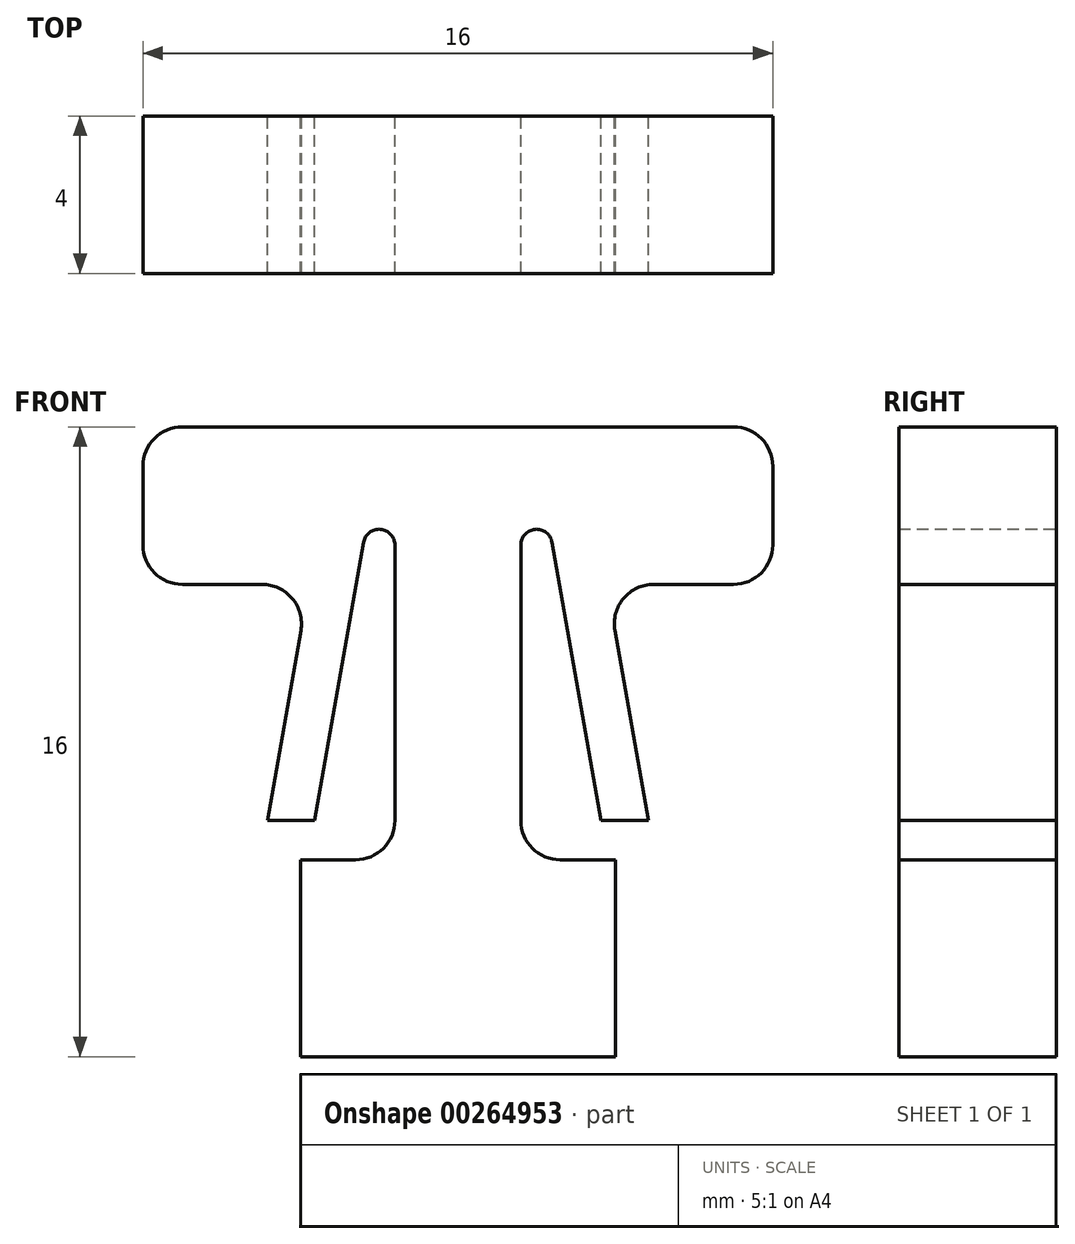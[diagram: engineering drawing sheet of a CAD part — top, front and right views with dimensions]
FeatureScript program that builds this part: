
annotation { "Feature Type Name" : "Feature", "Feature Type Description" : "" }
export const myFeature = defineFeature(function(context is Context, id is Id, definition is map)
    precondition{}
    {
        {
            var Q0;
            Q0=qCreatedBy(makeId("Front.planeOp"),FACE);
            var sketch = newSketch(context, id + "F0", { "sketchPlane" : qUnion([Q0])});
            skLineSegment(sketch, "E0", {"start": v(0, 0) * mm, "end": v(0, 25.15) * mm, "construction": true});
            skLineSegment(sketch, "E1", {"start": v(8, 16) * mm, "end": v(8, 12) * mm});
            skLineSegment(sketch, "E2", {"start": v(4.97, 12) * mm, "end": v(8, 12) * mm});
            skLineSegment(sketch, "E3", {"start": v(4, 0) * mm, "end": v(0, 0) * mm});
            skLineSegment(sketch, "E4", {"start": v(3.99, 10.83) * mm, "end": v(4.84, 6) * mm});
            skLineSegment(sketch, "E5", {"start": v(4.84, 6) * mm, "end": v(3.64, 6) * mm});
            skLineSegment(sketch, "E6", {"start": v(3.64, 6) * mm, "end": v(2.4, 13.07) * mm});
            skLineSegment(sketch, "E7", {"start": v(1.6, 13) * mm, "end": v(1.6, 5) * mm});
            skLineSegment(sketch, "E8", {"start": v(1.6, 5) * mm, "end": v(4, 5) * mm});
            skLineSegment(sketch, "E9", {"start": v(4, 5) * mm, "end": v(4, 0) * mm});
            skLineSegment(sketch, "E10", {"start": v(8, 16) * mm, "end": v(0, 16) * mm});
            skLineSegment(sketch, "E11.MirrorCS", {"start": v(-8, 16) * mm, "end": v(0, 16) * mm});
            skLineSegment(sketch, "E12.MirrorCS", {"start": v(-8, 16) * mm, "end": v(-8, 12) * mm});
            skLineSegment(sketch, "E13.MirrorCS", {"start": v(-4.97, 12) * mm, "end": v(-8, 12) * mm});
            skLineSegment(sketch, "E14.MirrorCS", {"start": v(-3.99, 10.83) * mm, "end": v(-4.84, 6) * mm});
            skLineSegment(sketch, "E15.MirrorCS", {"start": v(-4.84, 6) * mm, "end": v(-3.64, 6) * mm});
            skLineSegment(sketch, "E16.MirrorCS", {"start": v(-3.64, 6) * mm, "end": v(-2.4, 13.07) * mm});
            skLineSegment(sketch, "E17.MirrorCS", {"start": v(-1.6, 13) * mm, "end": v(-1.6, 5) * mm});
            skLineSegment(sketch, "E18.MirrorCS", {"start": v(-1.6, 5) * mm, "end": v(-4, 5) * mm});
            skLineSegment(sketch, "E19.MirrorCS", {"start": v(-4, 5) * mm, "end": v(-4, 0) * mm});
            skLineSegment(sketch, "E20.MirrorCS", {"start": v(-4, 0) * mm, "end": v(0, 0) * mm});
            skPoint(sketch, "E21.newPointA", {"position": v(-2.58, 12) * mm});
            skPoint(sketch, "E21.newPointB", {"position": v(-1.6, 20) * mm});
            skArc(sketch, "E21.filletArc", {"start": v(-1.6, 13) * mm, "mid": v(-1.97, 13.4) * mm, "end": v(-2.4, 13.07) * mm});
            skPoint(sketch, "E22.newPointA", {"position": v(1.6, 20) * mm});
            skPoint(sketch, "E22.newPointB", {"position": v(2.58, 12) * mm});
            skArc(sketch, "E22.filletArc", {"start": v(2.4, 13.07) * mm, "mid": v(1.97, 13.4) * mm, "end": v(1.6, 13) * mm});
            skPoint(sketch, "E23.visualSharp", {"position": v(-3.78, 12) * mm});
            skArc(sketch, "E23.filletArc", {"start": v(-3.99, 10.83) * mm, "mid": v(-4.2, 11.64) * mm, "end": v(-4.97, 12) * mm});
            skPoint(sketch, "E24.visualSharp", {"position": v(3.78, 12) * mm});
            skArc(sketch, "E24.filletArc", {"start": v(4.97, 12) * mm, "mid": v(4.2, 11.64) * mm, "end": v(3.99, 10.83) * mm});
            skLineSegment(sketch, "E25", {"start": v(-2, 13) * mm, "end": v(2, 13) * mm, "construction": true});
            skSolve(sketch);
        }
        {
            var Q0;
            Q0 = qSketchRegion(id + "F0", true);
            extrude(context, id + "F1", {"entities" : qUnion([Q0]), "depth" : 4 * mm});
        }
        {
            var Q0;
            Q0=makeQuery(id+"F1.opExtrude","SWEPT_EDGE",EDGE,{"disambiguationData":[OSD([sQuery(id+"F0.wireOp",EDGE,"E1"),sQuery(id+"F0.wireOp",EDGE,"E2")])]});
            var Q1;
            Q1=makeQuery(id+"F1.opExtrude","SWEPT_EDGE",EDGE,{"disambiguationData":[OSD([sQuery(id+"F0.wireOp",EDGE,"E1"),sQuery(id+"F0.wireOp",EDGE,"E10")])]});
            var Q2;
            Q2=makeQuery(id+"F1.opExtrude","SWEPT_EDGE",EDGE,{"disambiguationData":[OSD([sQuery(id+"F0.wireOp",EDGE,"E12.MirrorCS"),sQuery(id+"F0.wireOp",EDGE,"E13.MirrorCS")])]});
            var Q3;
            Q3=makeQuery(id+"F1.opExtrude","SWEPT_EDGE",EDGE,{"disambiguationData":[OSD([sQuery(id+"F0.wireOp",EDGE,"E11.MirrorCS"),sQuery(id+"F0.wireOp",EDGE,"E12.MirrorCS")])]});
            var Q4;
            Q4=makeQuery(id+"F1.opExtrude","SWEPT_EDGE",EDGE,{"disambiguationData":[OSD([sQuery(id+"F0.wireOp",EDGE,"E7"),sQuery(id+"F0.wireOp",EDGE,"E8")])]});
            var Q5;
            Q5=makeQuery(id+"F1.opExtrude","SWEPT_EDGE",EDGE,{"disambiguationData":[OSD([sQuery(id+"F0.wireOp",EDGE,"E17.MirrorCS"),sQuery(id+"F0.wireOp",EDGE,"E18.MirrorCS")])]});
            fillet(context, id + "F2", {"entities" : qUnion([Q0, Q1, Q2, Q3, Q4, Q5]), "radius" : 1 * mm, "tangentPropagation" : true, "allowEdgeOverflow" : false});
        }
    });
